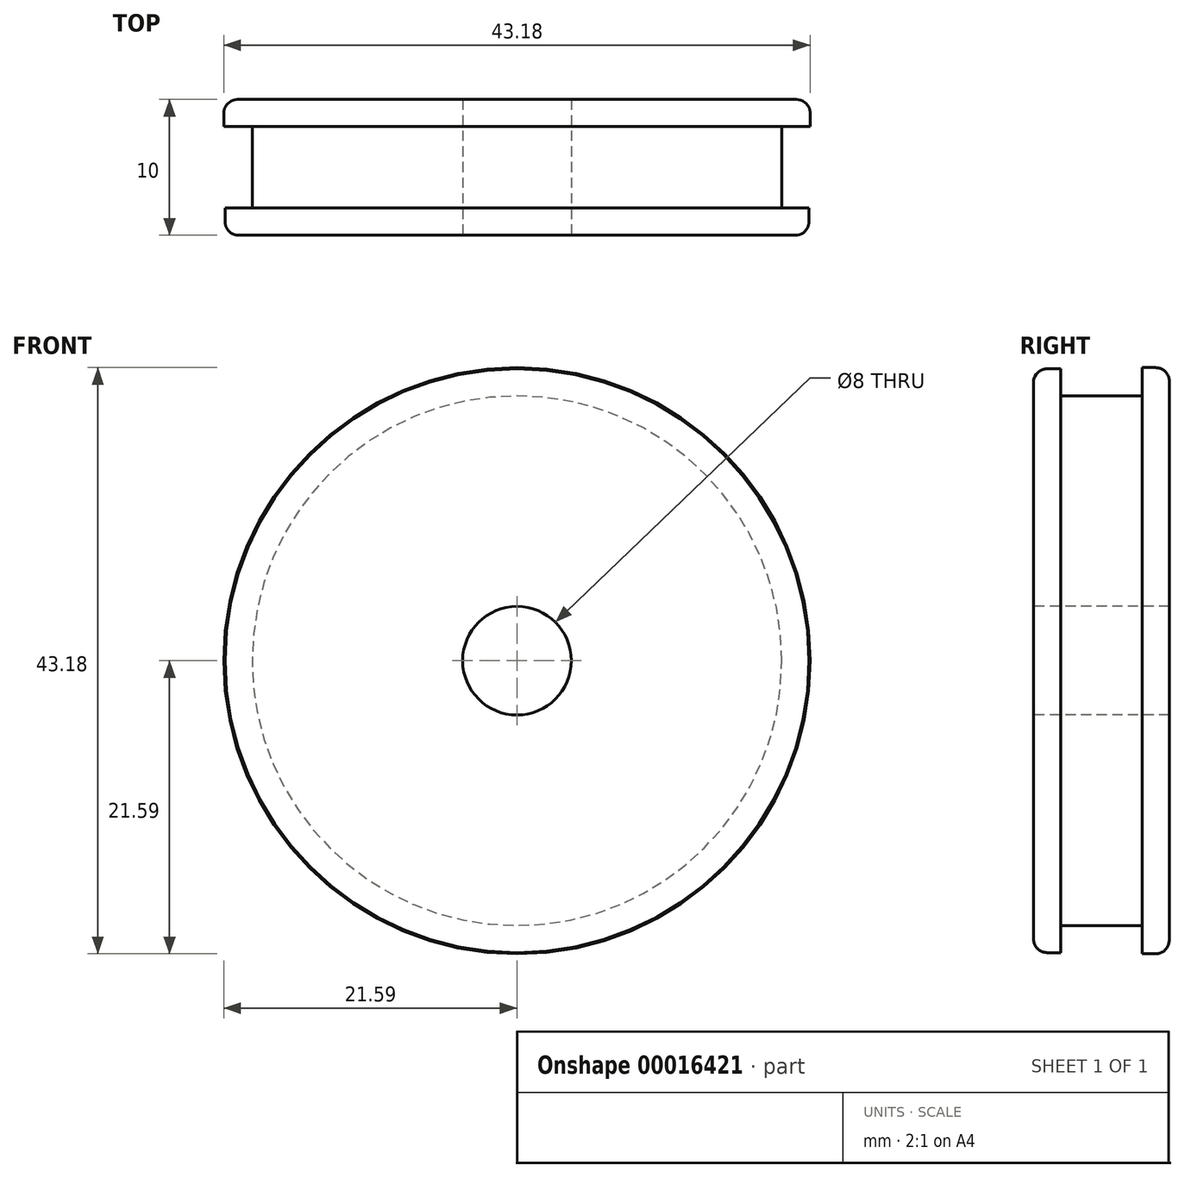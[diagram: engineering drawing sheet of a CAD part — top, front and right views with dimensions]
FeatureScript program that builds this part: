
annotation { "Feature Type Name" : "Feature", "Feature Type Description" : "" }
export const myFeature = defineFeature(function(context is Context, id is Id, definition is map)
    precondition{}
    {
        {
            var Q0;
            Q0=qCreatedBy(makeId("Right.planeOp"),FACE);
            var sketch = newSketch(context, id + "F0", { "sketchPlane" : qUnion([Q0])});
            skLineSegment(sketch, "E0", {"start": v(-5.74, 21.5) * mm, "end": v(-3.74, 21.5) * mm});
            skLineSegment(sketch, "E1", {"start": v(-3.74, 21.5) * mm, "end": v(-3.74, 19.5) * mm});
            skLineSegment(sketch, "E2", {"start": v(-3.74, 19.5) * mm, "end": v(2.26, 19.5) * mm});
            skLineSegment(sketch, "E3", {"start": v(2.26, 19.5) * mm, "end": v(2.26, 21.59) * mm});
            skLineSegment(sketch, "E4", {"start": v(2.26, 21.59) * mm, "end": v(4.26, 21.59) * mm});
            skLineSegment(sketch, "E5", {"start": v(4.26, 21.59) * mm, "end": v(4.26, 4) * mm});
            skLineSegment(sketch, "E6", {"start": v(-26.06, 0) * mm, "end": v(25.7, 0) * mm, "construction": true});
            skLineSegment(sketch, "E7.0", {"start": v(-5.74, 4) * mm, "end": v(4.26, 4) * mm});
            skLineSegment(sketch, "E8.trimOffspring", {"start": v(-5.74, 4) * mm, "end": v(-5.74, 21.5) * mm});
            skSolve(sketch);
        }
        {
            var Q0;
            Q0=makeQuery(id+"F0.imprint","IMPRINT",FACE,{"disambiguationData":[TD([[makeQuery(id+"F0.imprint","IMPRINT",EDGE,{"derivedFrom":sQuery(id+"F0.wireOp",EDGE,"E0")}),-1.0]])]});
            var Q1;
            Q1=sQuery(id+"F0.wireOp",EDGE,"E6");
            revolve(context, id + "F1", {"entities" : qUnion([Q0]), "axis" : qUnion([Q1]), "revolveType" : RevolveType.FULL});
        }
        {
            var Q0;
            Q0=makeQuery(id+"F1.opRevolve","SWEPT_EDGE",EDGE,{"disambiguationData":[OSD([sQuery(id+"F0.wireOp",EDGE,"E0"),sQuery(id+"F0.wireOp",EDGE,"E8.trimOffspring")])]});
            var Q1;
            Q1=makeQuery(id+"F1.opRevolve","SWEPT_EDGE",EDGE,{"disambiguationData":[OSD([sQuery(id+"F0.wireOp",EDGE,"E4"),sQuery(id+"F0.wireOp",EDGE,"E5")])]});
            fillet(context, id + "F2", {"entities" : qUnion([Q0, Q1]), "radius" : 1 * mm, "tangentPropagation" : true, "allowEdgeOverflow" : false});
        }
    });
